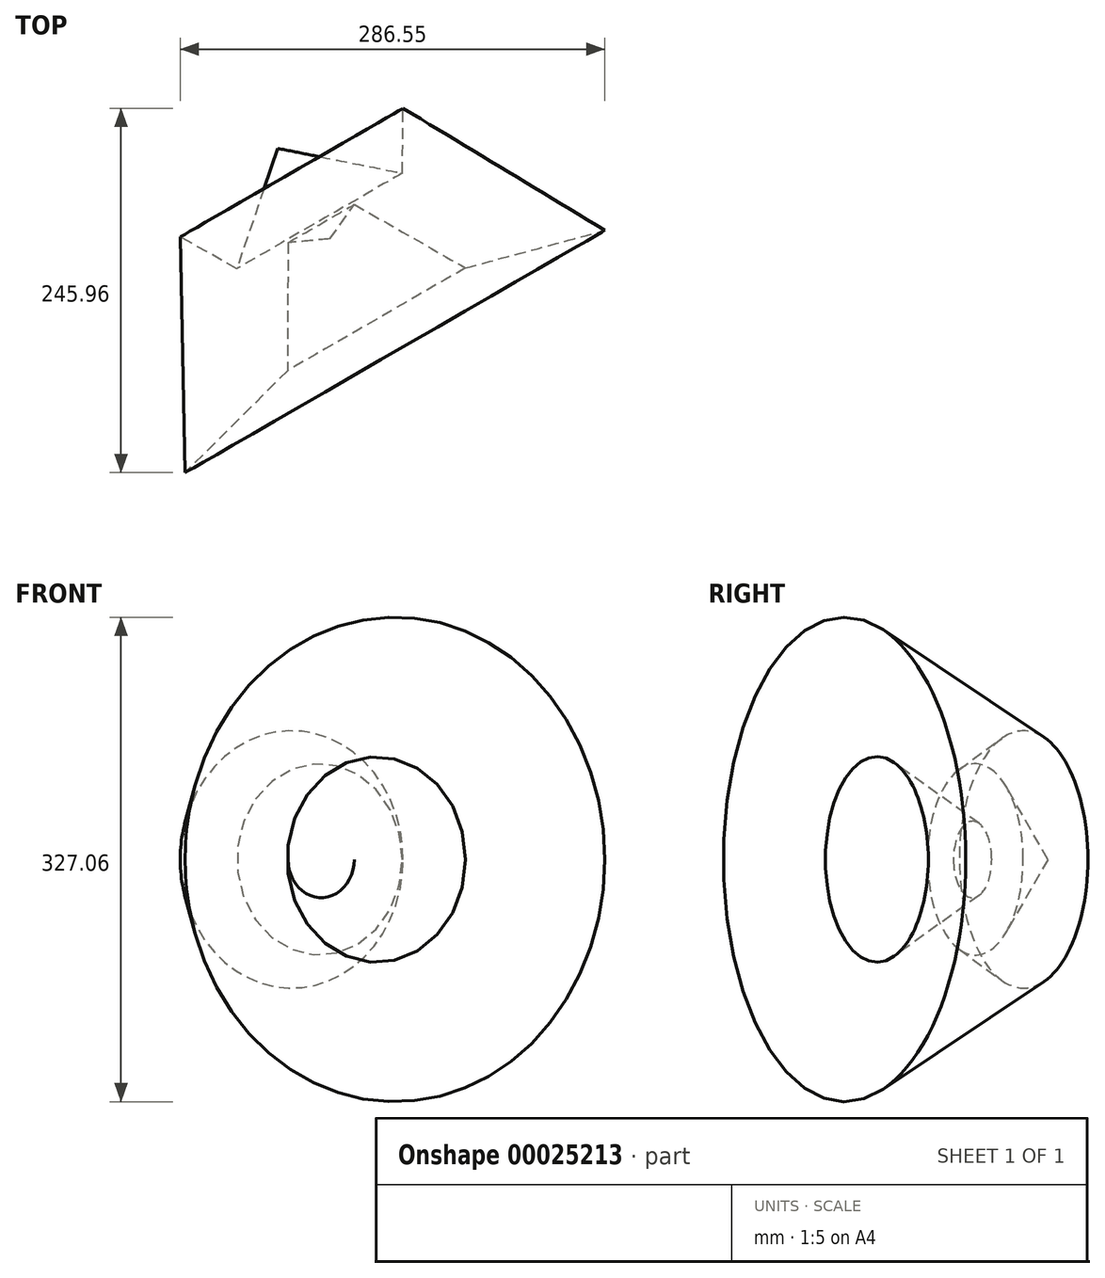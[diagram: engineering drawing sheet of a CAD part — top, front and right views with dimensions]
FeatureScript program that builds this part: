
annotation { "Feature Type Name" : "Feature", "Feature Type Description" : "" }
export const myFeature = defineFeature(function(context is Context, id is Id, definition is map)
    precondition{}
    {
        {
            var Q0;
            Q0=qCreatedBy(makeId("Top.planeOp"),FACE);
            var sketch = newSketch(context, id + "F0", { "sketchPlane" : qUnion([Q0])});
            skLineSegment(sketch, "E0", {"start": v(-43.83, -17.4) * mm, "end": v(-79.05, 43.6) * mm});
            skLineSegment(sketch, "E1", {"start": v(-79.05, 43.6) * mm, "end": v(5.06, 26.94) * mm});
            skLineSegment(sketch, "E2", {"start": v(5.06, 26.94) * mm, "end": v(5.56, 70.71) * mm});
            skLineSegment(sketch, "E3", {"start": v(5.56, 70.71) * mm, "end": v(141.73, -11.72) * mm});
            skLineSegment(sketch, "E4", {"start": v(141.73, -11.72) * mm, "end": v(47.64, -37.05) * mm});
            skLineSegment(sketch, "E5", {"start": v(47.64, -37.05) * mm, "end": v(-27.41, 5.78) * mm});
            skLineSegment(sketch, "E6", {"start": v(-27.41, 5.78) * mm, "end": v(-43.83, -17.4) * mm});
            skSolve(sketch);
        }
        {
            var Q0;
            Q0=makeQuery(id+"F0.imprint","IMPRINT",FACE,{"disambiguationData":[TD([[makeQuery(id+"F0.imprint","IMPRINT",EDGE,{"derivedFrom":sQuery(id+"F0.wireOp",EDGE,"E0")}),-1.0]])]});
            var Q1;
            Q1=sQuery(id+"F0.wireOp",EDGE,"E0");
            revolve(context, id + "F1", {"entities" : qUnion([Q0]), "axis" : qUnion([Q1]), "revolveType" : RevolveType.FULL});
        }
    });
